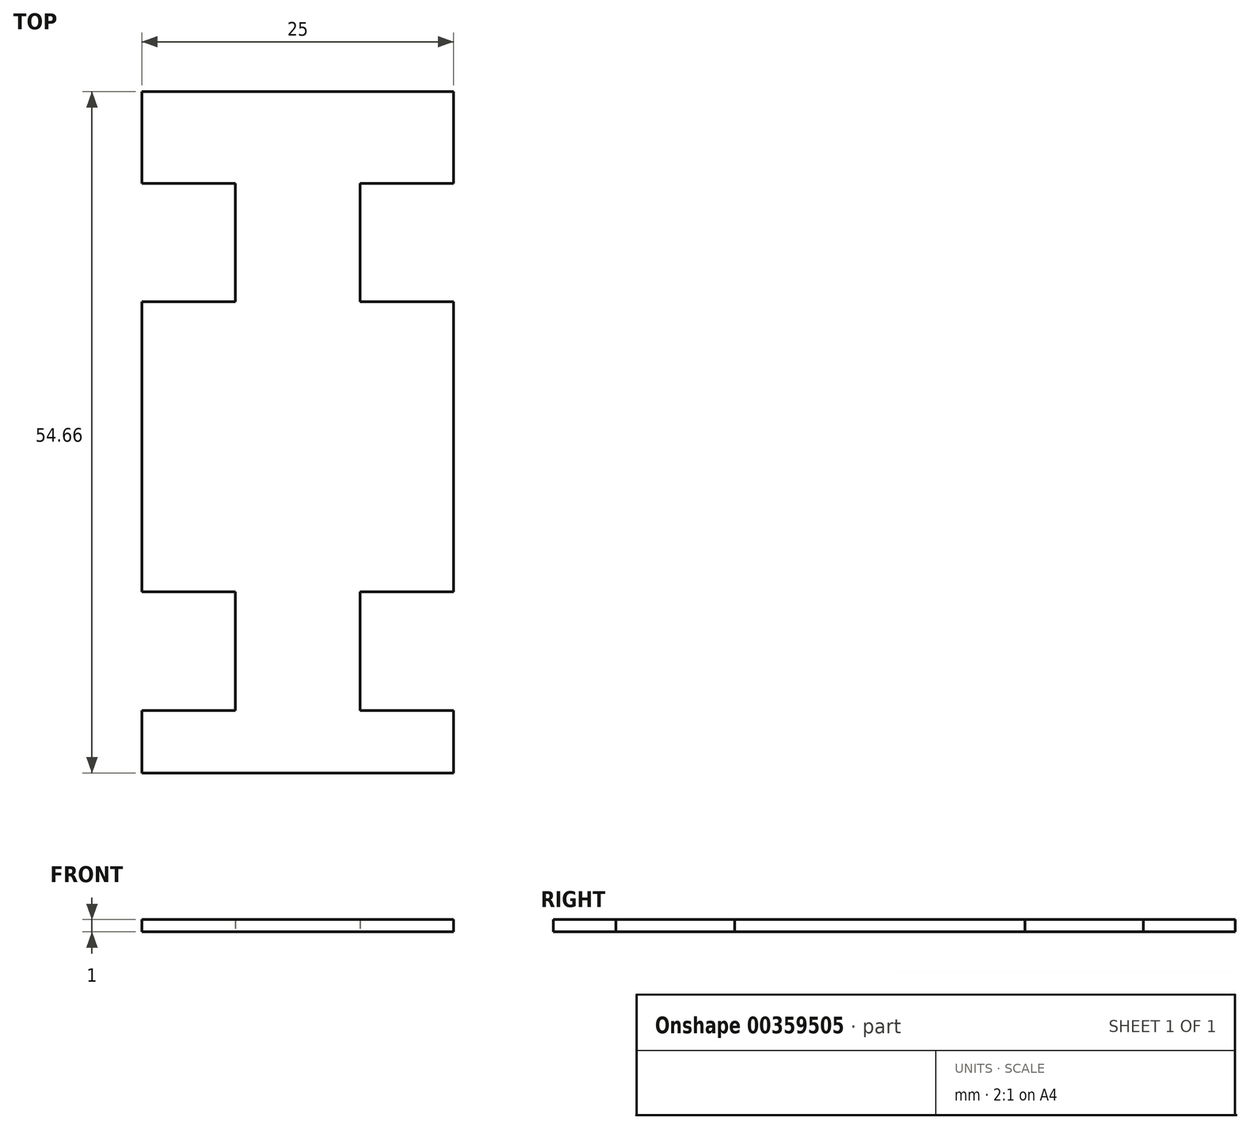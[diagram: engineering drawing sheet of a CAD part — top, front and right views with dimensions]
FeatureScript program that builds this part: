
annotation { "Feature Type Name" : "Feature", "Feature Type Description" : "" }
export const myFeature = defineFeature(function(context is Context, id is Id, definition is map)
    precondition{}
    {
        {
            var Q0;
            Q0=qCreatedBy(makeId("Top.planeOp"),FACE);
            var sketch = newSketch(context, id + "F0", { "sketchPlane" : qUnion([Q0])});
            skLineSegment(sketch, "E0.bottom", {"start": v(12.5, -27.33) * mm, "end": v(-12.5, -27.33) * mm});
            skLineSegment(sketch, "E0.top", {"start": v(12.5, 27.33) * mm, "end": v(-12.5, 27.33) * mm});
            skPoint(sketch, "E0.middle", {"position": v(0, 0) * mm});
            skLineSegment(sketch, "E1.bottom", {"start": v(-12.5, 19.97) * mm, "end": v(-5, 19.97) * mm});
            skLineSegment(sketch, "E1.top", {"start": v(-12.5, 10.47) * mm, "end": v(-5, 10.47) * mm});
            skLineSegment(sketch, "E1.right", {"start": v(-5, 19.97) * mm, "end": v(-5, 10.47) * mm});
            skLineSegment(sketch, "E2.bottom", {"start": v(12.5, 19.97) * mm, "end": v(5, 19.97) * mm});
            skLineSegment(sketch, "E2.top", {"start": v(12.5, 10.47) * mm, "end": v(5, 10.47) * mm});
            skLineSegment(sketch, "E2.right", {"start": v(5, 19.97) * mm, "end": v(5, 10.47) * mm});
            skLineSegment(sketch, "E3.bottom", {"start": v(-12.5, -12.8) * mm, "end": v(-5, -12.8) * mm});
            skLineSegment(sketch, "E3.top", {"start": v(-12.5, -22.3) * mm, "end": v(-5, -22.3) * mm});
            skLineSegment(sketch, "E3.right", {"start": v(-5, -12.8) * mm, "end": v(-5, -22.3) * mm});
            skLineSegment(sketch, "E4.bottom", {"start": v(12.5, -12.8) * mm, "end": v(5, -12.8) * mm});
            skLineSegment(sketch, "E4.top", {"start": v(12.5, -22.3) * mm, "end": v(5, -22.3) * mm});
            skLineSegment(sketch, "E4.right", {"start": v(5, -12.8) * mm, "end": v(5, -22.3) * mm});
            skLineSegment(sketch, "E5.trimOffspring", {"start": v(12.5, 19.97) * mm, "end": v(12.5, 27.33) * mm});
            skLineSegment(sketch, "E6", {"start": v(12.5, 10.47) * mm, "end": v(12.5, -12.8) * mm});
            skLineSegment(sketch, "E7.trimOffspring", {"start": v(-12.5, 19.97) * mm, "end": v(-12.5, 27.33) * mm});
            skLineSegment(sketch, "E8.trimOffspring", {"start": v(-12.5, -12.8) * mm, "end": v(-12.5, 10.47) * mm});
            skLineSegment(sketch, "E9", {"start": v(-12.5, -22.3) * mm, "end": v(-12.5, -27.33) * mm});
            skLineSegment(sketch, "E10", {"start": v(12.5, -22.3) * mm, "end": v(12.5, -27.33) * mm});
            skSolve(sketch);
        }
        {
            var Q0;
            Q0 = qSketchRegion(id + "F0", true);
            extrude(context, id + "F1", {"entities" : qUnion([Q0]), "depth" : 1 * mm});
        }
    });
